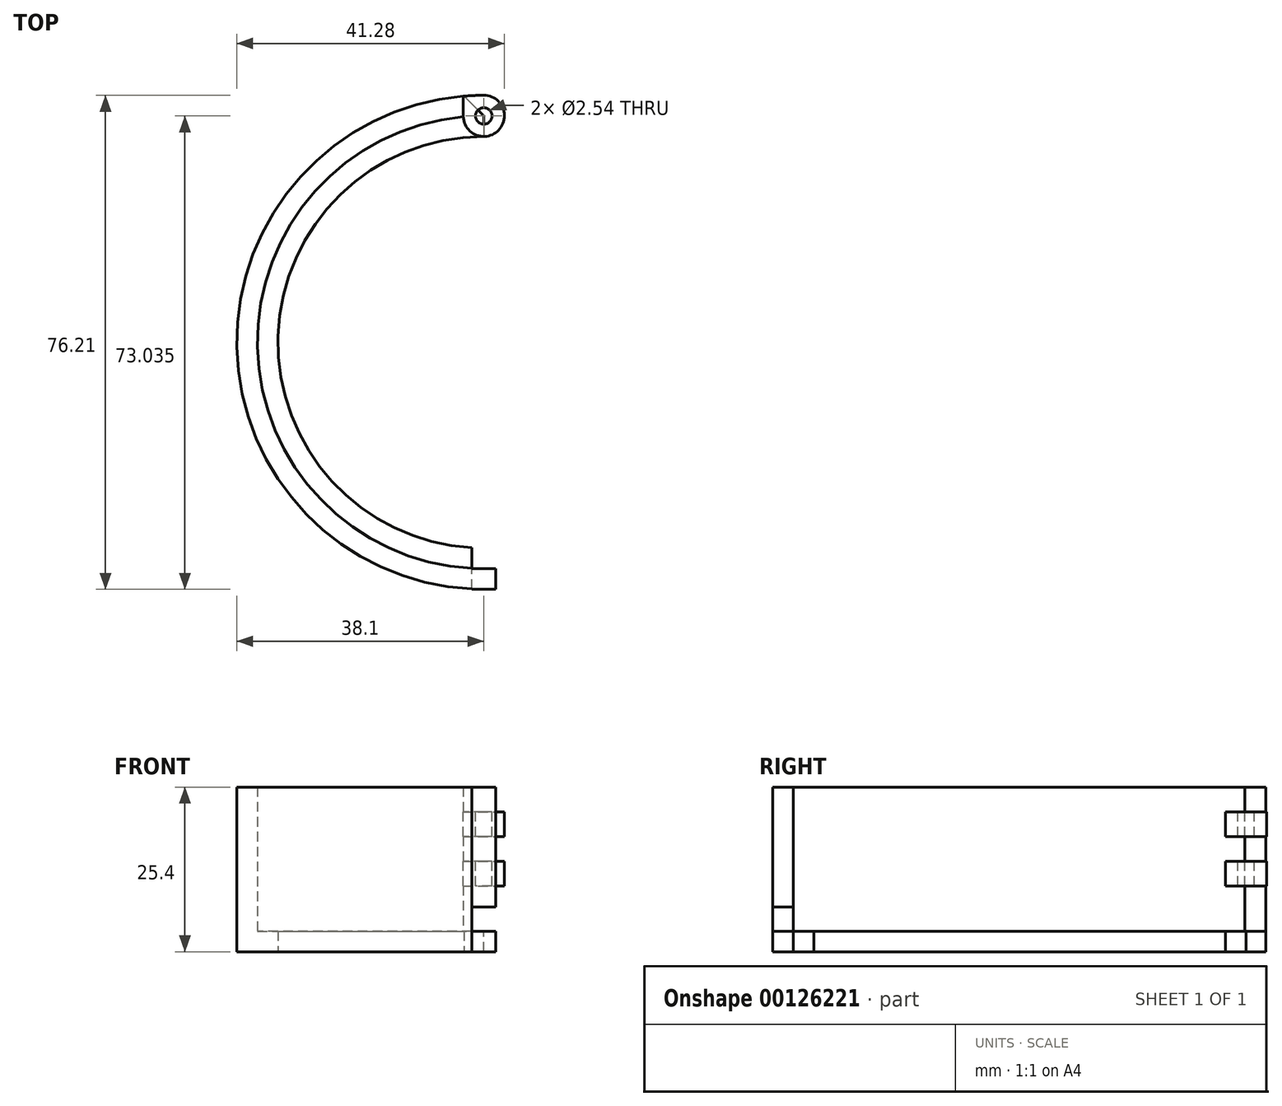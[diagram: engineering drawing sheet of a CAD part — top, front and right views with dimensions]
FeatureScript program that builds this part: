
annotation { "Feature Type Name" : "Feature", "Feature Type Description" : "" }
export const myFeature = defineFeature(function(context is Context, id is Id, definition is map)
    precondition{}
    {
        {
            var Q0;
            Q0=qCreatedBy(makeId("Front.planeOp"),FACE);
            var sketch = newSketch(context, id + "F0", { "sketchPlane" : qUnion([Q0])});
            skLineSegment(sketch, "E0", {"start": v(0, 0) * mm, "end": v(0, 25.4) * mm, "construction": true});
            skLineSegment(sketch, "E1", {"start": v(-31.75, 0) * mm, "end": v(-38.1, 0) * mm});
            skLineSegment(sketch, "E2", {"start": v(-38.1, 0) * mm, "end": v(-38.1, 25.4) * mm});
            skLineSegment(sketch, "E3", {"start": v(-38.1, 25.4) * mm, "end": v(-34.92, 25.4) * mm});
            skLineSegment(sketch, "E4", {"start": v(-34.92, 25.4) * mm, "end": v(-34.92, 3.17) * mm});
            skLineSegment(sketch, "E5", {"start": v(-34.92, 3.17) * mm, "end": v(-31.75, 3.17) * mm});
            skLineSegment(sketch, "E6", {"start": v(-31.75, 3.17) * mm, "end": v(-31.75, 0) * mm});
            skSolve(sketch);
        }
        {
            var Q0;
            Q0=qSketchRegion(id+"F0",true);
            var Q1;
            Q1=sQuery(id+"F0.wireOp",EDGE,"E0");
            revolve(context, id + "F1", {"entities" : qUnion([Q0]), "axis" : qUnion([Q1]), "revolveType" : RevolveType.FULL});
        }
        {
            var Q0;
            Q0=qCreatedBy(makeId("Front.planeOp"),FACE);
            cPlane(context, id + "F2", {"entities" : qUnion([Q0]), "cplaneType" : CPlaneType.OFFSET, "offset" : 38.1 * mm, "width" : 152.4 * mm, "height" : 152.4 * mm});
        }
        {
            var Q0;
            Q0=qCreatedBy(id+"F2.planeOp",FACE);
            var sketch = newSketch(context, id + "F3", { "sketchPlane" : qUnion([Q0])});
            skLineSegment(sketch, "E7", {"start": v(0, 0) * mm, "end": v(0, 25.4) * mm});
            skPoint(sketch, "E8", {"position": v(0, 3.18) * mm});
            skLineSegment(sketch, "E9.bottom", {"start": v(-1.85, 3.18) * mm, "end": v(0, 3.18) * mm});
            skLineSegment(sketch, "E9.top", {"start": v(-1.85, 6.88) * mm, "end": v(1.85, 6.88) * mm});
            skLineSegment(sketch, "E9.left", {"start": v(-1.85, 3.18) * mm, "end": v(-1.85, 6.88) * mm});
            skLineSegment(sketch, "E9.right", {"start": v(1.85, 3.18) * mm, "end": v(1.85, 6.88) * mm});
            skPoint(sketch, "E9.middle", {"position": v(0, 5.03) * mm});
            skLineSegment(sketch, "E10.top", {"start": v(-1.85, 10.58) * mm, "end": v(1.85, 10.58) * mm});
            skLineSegment(sketch, "E10.left", {"start": v(-1.85, 6.88) * mm, "end": v(-1.85, 10.58) * mm});
            skLineSegment(sketch, "E10.right", {"start": v(1.85, 6.88) * mm, "end": v(1.85, 10.58) * mm});
            skPoint(sketch, "E10.middle", {"position": v(0, 8.73) * mm});
            skLineSegment(sketch, "E11.top", {"start": v(-1.85, 14.29) * mm, "end": v(1.85, 14.29) * mm});
            skLineSegment(sketch, "E11.left", {"start": v(-1.85, 10.58) * mm, "end": v(-1.85, 14.29) * mm});
            skLineSegment(sketch, "E11.right", {"start": v(1.85, 10.58) * mm, "end": v(1.85, 14.29) * mm});
            skPoint(sketch, "E11.middle", {"position": v(0, 12.44) * mm});
            skLineSegment(sketch, "E12.top", {"start": v(-1.85, 18) * mm, "end": v(1.85, 18) * mm});
            skLineSegment(sketch, "E12.left", {"start": v(-1.85, 14.29) * mm, "end": v(-1.85, 18) * mm});
            skLineSegment(sketch, "E12.right", {"start": v(1.85, 14.29) * mm, "end": v(1.85, 18) * mm});
            skPoint(sketch, "E12.middle", {"position": v(0, 16.14) * mm});
            skLineSegment(sketch, "E13.top", {"start": v(-1.85, 21.7) * mm, "end": v(1.85, 21.7) * mm});
            skLineSegment(sketch, "E13.left", {"start": v(-1.85, 18) * mm, "end": v(-1.85, 21.7) * mm});
            skLineSegment(sketch, "E13.right", {"start": v(1.85, 18) * mm, "end": v(1.85, 21.7) * mm});
            skPoint(sketch, "E13.middle", {"position": v(0, 19.84) * mm});
            skLineSegment(sketch, "E14.top", {"start": v(-1.85, 25.4) * mm, "end": v(1.85, 25.4) * mm});
            skLineSegment(sketch, "E14.left", {"start": v(-1.85, 21.7) * mm, "end": v(-1.85, 25.4) * mm});
            skLineSegment(sketch, "E14.right", {"start": v(1.85, 21.7) * mm, "end": v(1.85, 25.4) * mm});
            skPoint(sketch, "E14.middle", {"position": v(0, 23.55) * mm});
            skLineSegment(sketch, "E15.left", {"start": v(-1.85, 25.4) * mm, "end": v(-1.85, 0) * mm});
            skLineSegment(sketch, "E16", {"start": v(0, 3.18) * mm, "end": v(1.85, 3.18) * mm});
            skLineSegment(sketch, "E17.bottom", {"start": v(1.85, 25.4) * mm, "end": v(50.8, 25.4) * mm});
            skLineSegment(sketch, "E17.top", {"start": v(1.85, 0) * mm, "end": v(50.8, 0) * mm});
            skLineSegment(sketch, "E17.left", {"start": v(1.85, 25.4) * mm, "end": v(1.85, 0) * mm});
            skLineSegment(sketch, "E17.right", {"start": v(50.8, 25.4) * mm, "end": v(50.8, 0) * mm});
            skLineSegment(sketch, "E18", {"start": v(-1.85, 0) * mm, "end": v(1.85, 0) * mm});
            skSolve(sketch);
        }
        {
            var Q0;
            {var subQ0=sQuery(id+"F3.wireOp",EDGE,"E9.bottom");Q0=makeQuery(id+"F3.imprint","IMPRINT",FACE,{"disambiguationData":[TD([[makeQuery(id+"F3.imprint","IMPRINT",EDGE,{"derivedFrom":subQ0}),1.0]])]});}
            var Q1;
            {var subQ0=sQuery(id+"F3.wireOp",EDGE,"E16");Q1=makeQuery(id+"F3.imprint","IMPRINT",FACE,{"disambiguationData":[TD([[makeQuery(id+"F3.imprint","IMPRINT",EDGE,{"derivedFrom":subQ0}),1.0]])]});}
            var Q2;
            {var subQ0=sQuery(id+"F3.wireOp",EDGE,"E10.top");var subQ1=sQuery(id+"F3.wireOp",EDGE,"E7");var subQ2=makeQuery(id+"F3.imprint","INTERSECT",VERTEX,{"derivedFrom":[subQ1,subQ0]});Q2=makeQuery(id+"F3.imprint","IMPRINT",FACE,{"disambiguationData":[TD([[makeQuery(id+"F3.imprint","IMPRINT",EDGE,{"disambiguationData":[TD([[subQ2,-1.0]])],"derivedFrom":subQ1}),-1.0]])]});}
            var Q3;
            {var subQ0=sQuery(id+"F3.wireOp",EDGE,"E10.top");var subQ1=sQuery(id+"F3.wireOp",EDGE,"E7");var subQ2=makeQuery(id+"F3.imprint","INTERSECT",VERTEX,{"derivedFrom":[subQ1,subQ0]});Q3=makeQuery(id+"F3.imprint","IMPRINT",FACE,{"disambiguationData":[TD([[makeQuery(id+"F3.imprint","IMPRINT",EDGE,{"disambiguationData":[TD([[subQ2,-1.0]])],"derivedFrom":subQ1}),1.0]])]});}
            var Q4;
            {var subQ0=sQuery(id+"F3.wireOp",EDGE,"E12.top");var subQ1=sQuery(id+"F3.wireOp",EDGE,"E7");var subQ2=makeQuery(id+"F3.imprint","INTERSECT",VERTEX,{"derivedFrom":[subQ1,subQ0]});Q4=makeQuery(id+"F3.imprint","IMPRINT",FACE,{"disambiguationData":[TD([[makeQuery(id+"F3.imprint","IMPRINT",EDGE,{"disambiguationData":[TD([[subQ2,-1.0]])],"derivedFrom":subQ1}),1.0]])]});}
            var Q5;
            {var subQ2=sQuery(id+"F3.wireOp",EDGE,"E17.bottom");Q5=makeQuery(id+"F3.imprint","IMPRINT",FACE,{"disambiguationData":[TD([[makeQuery(id+"F3.imprint","IMPRINT",EDGE,{"derivedFrom":subQ2}),-1.0]])]});}
            var Q6;
            {var subQ0=sQuery(id+"F3.wireOp",EDGE,"E12.top");var subQ1=sQuery(id+"F3.wireOp",EDGE,"E7");var subQ2=makeQuery(id+"F3.imprint","INTERSECT",VERTEX,{"derivedFrom":[subQ1,subQ0]});Q6=makeQuery(id+"F3.imprint","IMPRINT",FACE,{"disambiguationData":[TD([[makeQuery(id+"F3.imprint","IMPRINT",EDGE,{"disambiguationData":[TD([[subQ2,-1.0]])],"derivedFrom":subQ1}),-1.0]])]});}
            var Q7;
            {var subQ3=sQuery(id+"F3.wireOp",EDGE,"E16");Q7=makeQuery(id+"F3.imprint","IMPRINT",FACE,{"disambiguationData":[TD([[makeQuery(id+"F3.imprint","IMPRINT",EDGE,{"derivedFrom":subQ3}),-1.0]])]});}
            var Q8;
            {var subQ3=sQuery(id+"F3.wireOp",EDGE,"E9.bottom");Q8=makeQuery(id+"F3.imprint","IMPRINT",FACE,{"disambiguationData":[TD([[makeQuery(id+"F3.imprint","IMPRINT",EDGE,{"derivedFrom":subQ3}),-1.0]])]});}
            extrude(context, id + "F4", {"entities" : qUnion([Q0, Q1, Q2, Q3, Q4, Q5, Q6, Q7, Q8]), "operationType" : NewBodyOperationType.REMOVE, "endBound" : BoundingType.SYMMETRIC, "oppositeDirection" : true, "depth" : 76.2 * mm});
        }
        {
            var Q0;
            Q0=makeQuery(id+"F1.opRevolve","SWEPT_FACE",FACE,{"disambiguationData":[OSD([sQuery(id+"F0.wireOp",EDGE,"E3")])]});
            var sketch = newSketch(context, id + "F5", { "sketchPlane" : qUnion([Q0])});
            skLineSegment(sketch, "E19", {"start": v(0, 38.1) * mm, "end": v(0, 31.75) * mm, "construction": true});
            skArc(sketch, "E20", {"start": v(0, 31.75) * mm, "mid": v(3.17, 34.92) * mm, "end": v(0, 38.1) * mm});
            skArc(sketch, "E21", {"start": v(31.75, 0) * mm, "mid": v(22.45, 22.45) * mm, "end": v(0, 31.75) * mm});
            skLineSegment(sketch, "E22", {"start": v(31.75, 0) * mm, "end": v(41.27, 0) * mm});
            skArc(sketch, "E23", {"start": v(0, 38.1) * mm, "mid": v(-1.53, 38.07) * mm, "end": v(-3.05, 37.98) * mm});
            skArc(sketch, "E24", {"start": v(41.27, 0) * mm, "mid": v(27.01, 31.2) * mm, "end": v(-5.92, 40.85) * mm});
            skLineSegment(sketch, "E25", {"start": v(0, 34.92) * mm, "end": v(-3.05, 37.98) * mm, "construction": true});
            skLineSegment(sketch, "E26", {"start": v(-3.05, 37.98) * mm, "end": v(-5.92, 40.85) * mm});
            skSolve(sketch);
        }
        {
            var Q0;
            Q0=qSketchRegion(id+"F5",true);
            extrude(context, id + "F6", {"entities" : qUnion([Q0]), "operationType" : NewBodyOperationType.REMOVE, "endBound" : BoundingType.THROUGH_ALL, "oppositeDirection" : true, "depth" : 25.4 * mm});
        }
        {
            var Q0;
            Q0=makeQuery(id+"F1.opRevolve","SWEPT_FACE",FACE,{"disambiguationData":[OSD([sQuery(id+"F0.wireOp",EDGE,"E3")])]});
            var sketch = newSketch(context, id + "F7", { "sketchPlane" : qUnion([Q0])});
            skCircle(sketch, "E27", {"center": v(0, 34.92) * mm, "radius": 3.17 * mm});
            skSolve(sketch);
        }
        {
            var Q0;
            Q0=qSketchRegion(id+"F7",true);
            extrude(context, id + "F8", {"entities" : qUnion([Q0]), "operationType" : NewBodyOperationType.ADD, "oppositeDirection" : true, "depth" : 15.24 * mm});
        }
        {
            var Q0;
            Q0=makeQuery(id+"F1.opRevolve","SWEPT_FACE",FACE,{"disambiguationData":[OSD([sQuery(id+"F0.wireOp",EDGE,"E3")])]});
            var sketch = newSketch(context, id + "F9", { "sketchPlane" : qUnion([Q0])});
            skCircle(sketch, "E28", {"center": v(0, 34.92) * mm, "radius": 1.27 * mm});
            skSolve(sketch);
        }
        {
            var Q0;
            Q0=qSketchRegion(id+"F9",true);
            extrude(context, id + "F10", {"entities" : qUnion([Q0]), "operationType" : NewBodyOperationType.REMOVE, "oppositeDirection" : true, "depth" : 22.22 * mm});
        }
        {
            var Q0;
            Q0=qCreatedBy(makeId("Right.planeOp"),FACE);
            var sketch = newSketch(context, id + "F11", { "sketchPlane" : qUnion([Q0])});
            skLineSegment(sketch, "E29", {"start": v(34.92, 0) * mm, "end": v(34.92, 25.4) * mm});
            skLineSegment(sketch, "E30.bottom", {"start": v(31.75, 10.16) * mm, "end": v(38.1, 10.16) * mm});
            skLineSegment(sketch, "E30.top", {"start": v(31.75, 3.17) * mm, "end": v(38.1, 3.17) * mm});
            skLineSegment(sketch, "E30.left", {"start": v(31.75, 10.16) * mm, "end": v(31.75, 3.17) * mm});
            skLineSegment(sketch, "E30.right", {"start": v(38.1, 10.16) * mm, "end": v(38.1, 3.17) * mm});
            skPoint(sketch, "E30.middle", {"position": v(34.93, 6.67) * mm});
            skLineSegment(sketch, "E31", {"start": v(38.1, 10.16) * mm, "end": v(38.1, 13.97) * mm});
            skLineSegment(sketch, "E32", {"start": v(38.1, 13.97) * mm, "end": v(38.1, 17.78) * mm});
            skLineSegment(sketch, "E33", {"start": v(38.1, 17.78) * mm, "end": v(38.1, 21.6) * mm});
            skLineSegment(sketch, "E34", {"start": v(38.1, 21.6) * mm, "end": v(38.1, 25.4) * mm});
            skLineSegment(sketch, "E35", {"start": v(31.75, 10.16) * mm, "end": v(31.75, 25.4) * mm});
            skLineSegment(sketch, "E36", {"start": v(38.1, 25.4) * mm, "end": v(31.75, 25.4) * mm});
            skLineSegment(sketch, "E37", {"start": v(38.1, 21.6) * mm, "end": v(31.75, 21.6) * mm});
            skLineSegment(sketch, "E38", {"start": v(38.1, 17.78) * mm, "end": v(31.75, 17.78) * mm});
            skLineSegment(sketch, "E39", {"start": v(38.1, 13.97) * mm, "end": v(31.75, 13.97) * mm});
            skSolve(sketch);
        }
        {
            var Q0;
            {var subQ5=sQuery(id+"F11.wireOp",EDGE,"E34");Q0=makeQuery(id+"F11.imprint","IMPRINT",FACE,{"disambiguationData":[TD([[makeQuery(id+"F11.imprint","IMPRINT",EDGE,{"derivedFrom":subQ5}),1.0]])]});}
            var Q1;
            {var subQ0=sQuery(id+"F11.wireOp",EDGE,"E36");var subQ1=sQuery(id+"F11.wireOp",EDGE,"E29");var subQ2=makeQuery(id+"F11.imprint","INTERSECT",VERTEX,{"derivedFrom":[subQ1,subQ0]});Q1=makeQuery(id+"F11.imprint","IMPRINT",FACE,{"disambiguationData":[TD([[makeQuery(id+"F11.imprint","IMPRINT",EDGE,{"disambiguationData":[TD([[subQ2,1.0]])],"derivedFrom":subQ1}),1.0]])]});}
            var Q2;
            {var subQ5=sQuery(id+"F11.wireOp",EDGE,"E32");Q2=makeQuery(id+"F11.imprint","IMPRINT",FACE,{"disambiguationData":[TD([[makeQuery(id+"F11.imprint","IMPRINT",EDGE,{"derivedFrom":subQ5}),1.0]])]});}
            var Q3;
            {var subQ5=sQuery(id+"F11.wireOp",EDGE,"E30.right");Q3=makeQuery(id+"F11.imprint","IMPRINT",FACE,{"disambiguationData":[TD([[makeQuery(id+"F11.imprint","IMPRINT",EDGE,{"derivedFrom":subQ5}),-1.0]])]});}
            var Q4;
            {var subQ5=sQuery(id+"F11.wireOp",EDGE,"E30.left");Q4=makeQuery(id+"F11.imprint","IMPRINT",FACE,{"disambiguationData":[TD([[makeQuery(id+"F11.imprint","IMPRINT",EDGE,{"derivedFrom":subQ5}),1.0]])]});}
            var Q5;
            {var subQ0=sQuery(id+"F11.wireOp",EDGE,"E39");var subQ1=sQuery(id+"F11.wireOp",EDGE,"E29");var subQ2=makeQuery(id+"F11.imprint","INTERSECT",VERTEX,{"derivedFrom":[subQ1,subQ0]});Q5=makeQuery(id+"F11.imprint","IMPRINT",FACE,{"disambiguationData":[TD([[makeQuery(id+"F11.imprint","IMPRINT",EDGE,{"disambiguationData":[TD([[subQ2,-1.0]])],"derivedFrom":subQ1}),1.0]])]});}
            extrude(context, id + "F12", {"entities" : qUnion([Q0, Q1, Q2, Q3, Q4, Q5]), "operationType" : NewBodyOperationType.REMOVE, "endBound" : BoundingType.SYMMETRIC, "oppositeDirection" : true, "depth" : 6.35 * mm});
        }
        {
            var Q0;
            {var subQ0=sQuery(id+"F3.wireOp",EDGE,"E9.top");var subQ1=sQuery(id+"F3.wireOp",EDGE,"E7");var subQ2=makeQuery(id+"F3.imprint","INTERSECT",VERTEX,{"derivedFrom":[subQ1,subQ0]});Q0=makeQuery(id+"F3.imprint","IMPRINT",FACE,{"disambiguationData":[TD([[makeQuery(id+"F3.imprint","IMPRINT",EDGE,{"disambiguationData":[TD([[subQ2,-1.0]])],"derivedFrom":subQ1}),1.0]])]});}
            var Q1;
            {var subQ0=sQuery(id+"F3.wireOp",EDGE,"E9.top");var subQ1=sQuery(id+"F3.wireOp",EDGE,"E7");var subQ2=makeQuery(id+"F3.imprint","INTERSECT",VERTEX,{"derivedFrom":[subQ1,subQ0]});Q1=makeQuery(id+"F3.imprint","IMPRINT",FACE,{"disambiguationData":[TD([[makeQuery(id+"F3.imprint","IMPRINT",EDGE,{"disambiguationData":[TD([[subQ2,-1.0]])],"derivedFrom":subQ1}),-1.0]])]});}
            var Q2;
            {var subQ0=sQuery(id+"F3.wireOp",EDGE,"E11.top");var subQ1=sQuery(id+"F3.wireOp",EDGE,"E7");var subQ2=makeQuery(id+"F3.imprint","INTERSECT",VERTEX,{"derivedFrom":[subQ1,subQ0]});Q2=makeQuery(id+"F3.imprint","IMPRINT",FACE,{"disambiguationData":[TD([[makeQuery(id+"F3.imprint","IMPRINT",EDGE,{"disambiguationData":[TD([[subQ2,-1.0]])],"derivedFrom":subQ1}),1.0]])]});}
            var Q3;
            {var subQ0=sQuery(id+"F3.wireOp",EDGE,"E11.top");var subQ1=sQuery(id+"F3.wireOp",EDGE,"E7");var subQ2=makeQuery(id+"F3.imprint","INTERSECT",VERTEX,{"derivedFrom":[subQ1,subQ0]});Q3=makeQuery(id+"F3.imprint","IMPRINT",FACE,{"disambiguationData":[TD([[makeQuery(id+"F3.imprint","IMPRINT",EDGE,{"disambiguationData":[TD([[subQ2,-1.0]])],"derivedFrom":subQ1}),-1.0]])]});}
            var Q4;
            {var subQ0=sQuery(id+"F3.wireOp",EDGE,"E14.top");var subQ1=sQuery(id+"F3.wireOp",EDGE,"E7");var subQ2=makeQuery(id+"F3.imprint","INTERSECT",VERTEX,{"derivedFrom":[subQ1,subQ0]});Q4=makeQuery(id+"F3.imprint","IMPRINT",FACE,{"disambiguationData":[TD([[makeQuery(id+"F3.imprint","IMPRINT",EDGE,{"disambiguationData":[TD([[subQ2,1.0]])],"derivedFrom":subQ1}),1.0]])]});}
            var Q5;
            {var subQ0=sQuery(id+"F3.wireOp",EDGE,"E14.top");var subQ1=sQuery(id+"F3.wireOp",EDGE,"E7");var subQ2=makeQuery(id+"F3.imprint","INTERSECT",VERTEX,{"derivedFrom":[subQ1,subQ0]});Q5=makeQuery(id+"F3.imprint","IMPRINT",FACE,{"disambiguationData":[TD([[makeQuery(id+"F3.imprint","IMPRINT",EDGE,{"disambiguationData":[TD([[subQ2,1.0]])],"derivedFrom":subQ1}),-1.0]])]});}
            extrude(context, id + "F13", {"entities" : qUnion([Q0, Q1, Q2, Q3, Q4, Q5]), "operationType" : NewBodyOperationType.ADD, "depth" : 3 / 406.4 * mm, "hasSecondDirection" : true, "secondDirectionOppositeDirection" : true, "secondDirectionDepth" : 3.17 * mm});
        }
        {
            var Q0;
            Q0=makeQuery(id+"F1.opRevolve","SWEPT_FACE",FACE,{"disambiguationData":[OSD([sQuery(id+"F0.wireOp",EDGE,"E1")])]});
            var sketch = newSketch(context, id + "F14", { "sketchPlane" : qUnion([Q0])});
            skLineSegment(sketch, "E40", {"start": v(0, -34.93) * mm, "end": v(0, -31.75) * mm});
            skLineSegment(sketch, "E41.trimOffspring", {"start": v(0, -31.75) * mm, "end": v(0, -31.75) * mm});
            skLineSegment(sketch, "E42", {"start": v(0, -31.75) * mm, "end": v(0, -34.93) * mm});
            skArc(sketch, "E43", {"start": v(0, -38.1) * mm, "mid": v(3.17, -34.93) * mm, "end": v(0, -31.75) * mm});
            skLineSegment(sketch, "E44", {"start": v(0, -38.1) * mm, "end": v(0, -38.1) * mm});
            skLineSegment(sketch, "E45", {"start": v(0, -34.92) * mm, "end": v(-3.05, -37.98) * mm});
            skArc(sketch, "E46", {"start": v(-3.05, -37.98) * mm, "mid": v(-1.53, -38.07) * mm, "end": v(0, -38.1) * mm});
            skSolve(sketch);
        }
        {
            var Q0;
            Q0 = qSketchRegion(id + "F14", true);
            var Q1;
            {var subQ4=sQuery(id+"F14.wireOp",EDGE,"E41.trimOffspring");Q1=makeQuery(id+"F14.imprint","IMPRINT",FACE,{"disambiguationData":[TD([[makeQuery(id+"F14.imprint","IMPRINT",EDGE,{"derivedFrom":subQ4}),1.0]])]});}
            extrude(context, id + "F15", {"entities" : qUnion([Q0, Q1]), "operationType" : NewBodyOperationType.REMOVE, "oppositeDirection" : true, "depth" : 3.17 * mm});
        }
    });
